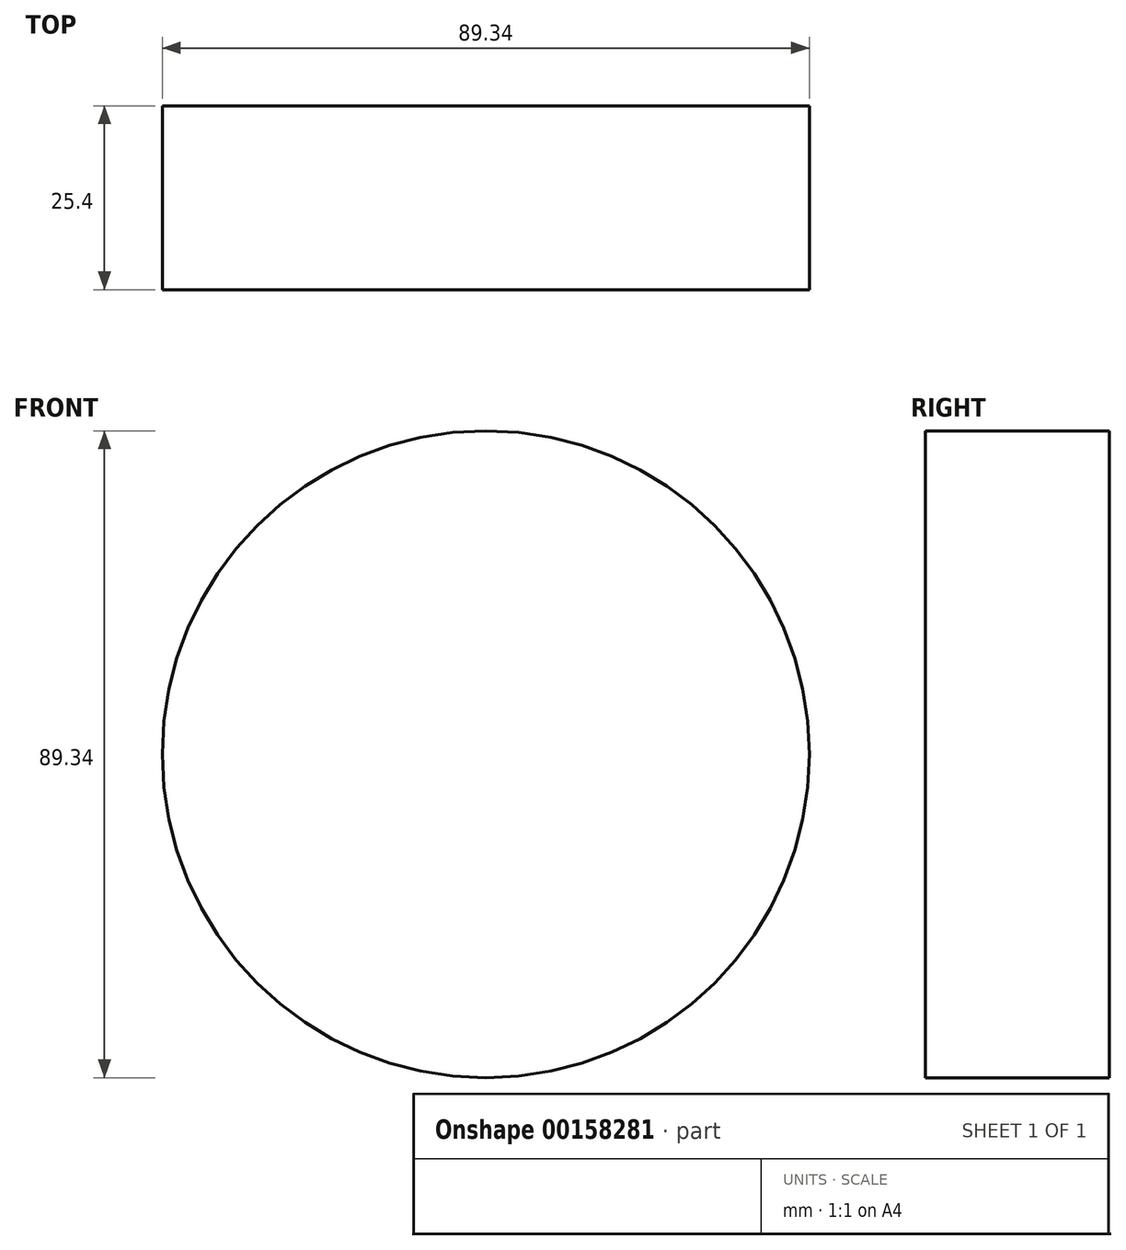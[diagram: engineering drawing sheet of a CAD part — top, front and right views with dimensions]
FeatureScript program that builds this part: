
annotation { "Feature Type Name" : "Feature", "Feature Type Description" : "" }
export const myFeature = defineFeature(function(context is Context, id is Id, definition is map)
    precondition{}
    {
        {
            var Q0;
            Q0=qCreatedBy(makeId("Front.planeOp"),FACE);
            var sketch = newSketch(context, id + "F0", { "sketchPlane" : qUnion([Q0])});
            skCircle(sketch, "E0", {"center": v(0, 0) * mm, "radius": 44.67 * mm});
            skSolve(sketch);
        }
        {
            var Q0;
            Q0 = qSketchRegion(id + "F0", true);
            extrude(context, id + "F1", {"entities" : qUnion([Q0]), "depth" : 25.4 * mm});
        }
    });
